# Revit family: Furniture_Other_Sjobergs_Workbench_Square
name_source: partatom
category: Furniture
revit_build: Autodesk Revit 2017 (Build: 20190508_0315(x64)
units: mm (PartAtom-declared; Revit-internal decimal feet)

## family parameters
Always vertical = Yes
Cut with Voids When Loaded = No
OmniClass Number = 23.40.70.14
OmniClass Title = Retail and Commercial Equipment and Furnishings
Room Calculation Point = No
Shared = No
Work Plane-Based = No

## types (1)
- 33072 Sjoberg Complete Square
    AssetType = Movable
    BIMObjectName = Furniture_Other_Sjobergs_Workbench_Square
    Brand = Sjöbergs
    Category = School, Woodwork
    Collection = Planer Benches
    Color = Wooden
    Constituents = 33797 bench top + 33198 steel stand + 33183 additional board + 33142 gas springs + 33383 jaw cushions + 33200 hinged stool + 33636 holdfast
    ConvergoRefNr = 0184-2005-0002-SE
    Cost = 0 $
    DurationUnit = Year
    Features = Provides 4 working places. The external dimensions of the Kvadraten are 1300x1300x60 mm. The top is supplied with a double row of holes for the round bench dogs to provide more flexible clamping. Bench dogs are included.
    Finish = Lacquered beech.
    IfcExportAs = IfcFurnishingElementType
    IfcExportType = TABLE
    MainColor = Wooden
    Manufacturer = Sjöbergs
    ManufacturerName = Sjöbergs
    ManufacturerURL = https://www.sjobergs.se
    Material = Wood, metal
    Model = 33072 Sjoberg Complete Square
    ModelReference = 33072
    NBSDescription = School art, design and technology tables and workbenches;
    NBSReference = 45-35-20/320
    Name = Sjobergs_Workbench_Square
    NominalDepth = 1584 mm
    NominalLength = 1584 mm
    ProductDatasheet = https://www.sjobergs.se
    Shape = Sculptured
    Size = 1584x1584x700-900 mm
    TableMainMaterial = Beech
    TableSecondaryMaterial = Stainless Steel
    TableTertiaryMaterial = Ash
    URL = https://www.sjobergs.se
    Uniclass2 = Pr_40_50_21
    Uniclass2015Description = Desks, Tables And Worktops
    Uniclass2015Reference = Pr_40_50_21_76
    Version = 1
    VersionDate = 26/06/2020
    WarrantyDurationUnit = Year
    Weight = 133 kg

## geometry (parser evidence)
native form markers: Sweep x10
no freeform markers — native parametric forms only
